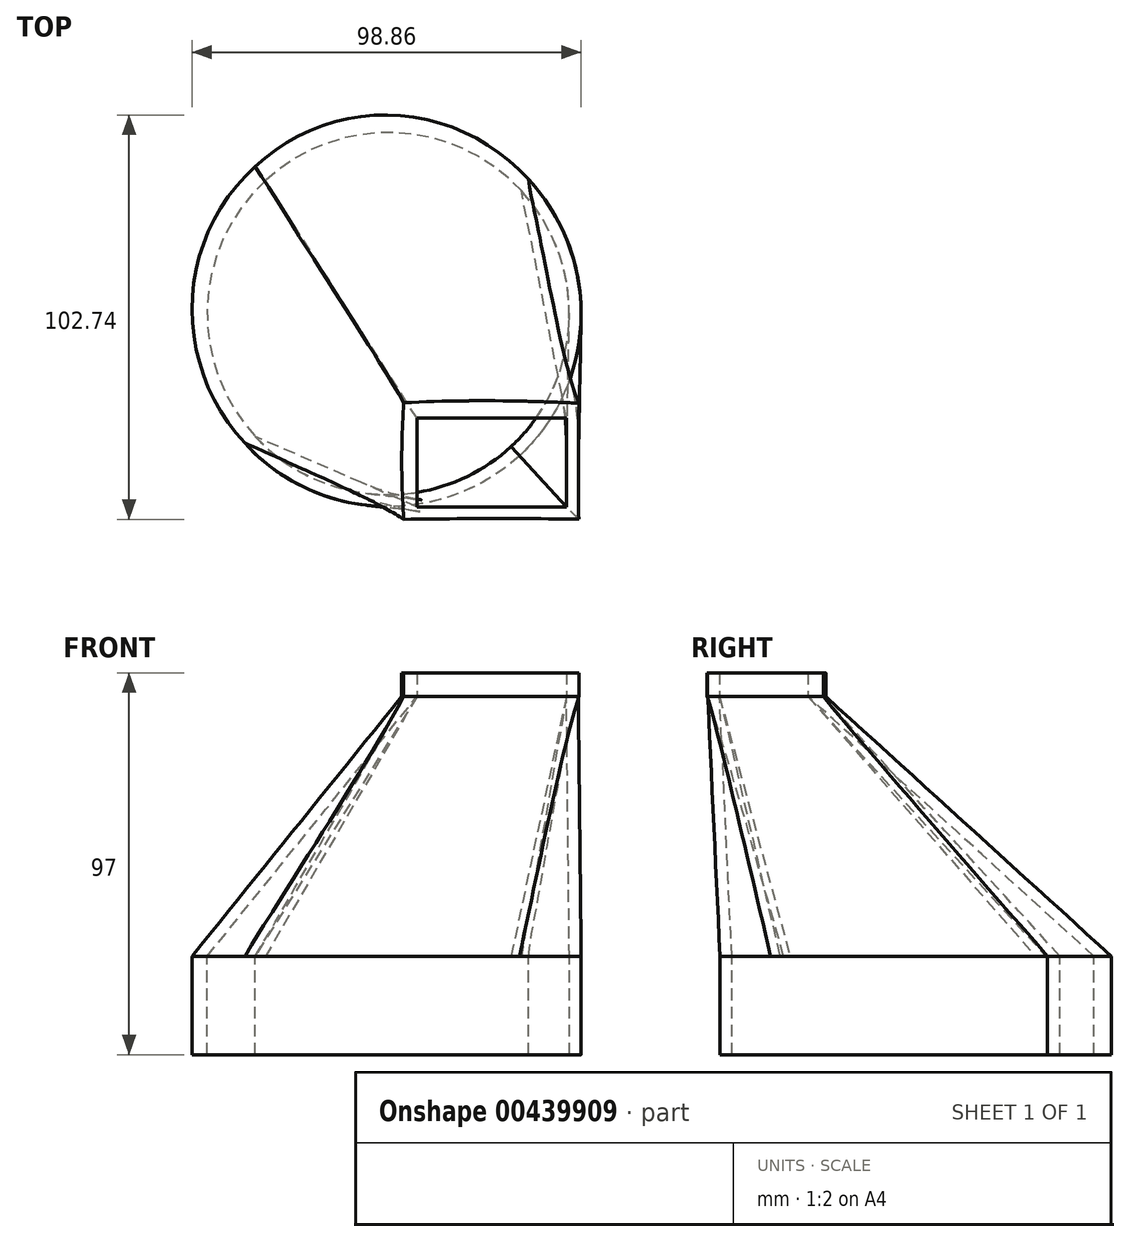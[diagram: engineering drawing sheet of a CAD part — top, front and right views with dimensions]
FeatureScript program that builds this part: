
annotation { "Feature Type Name" : "Feature", "Feature Type Description" : "" }
export const myFeature = defineFeature(function(context is Context, id is Id, definition is map)
    precondition{}
    {
        {
            var Q0;
            Q0=qCreatedBy(makeId("Top.planeOp"),FACE);
            cPlane(context, id + "F0", {"entities" : qUnion([Q0]), "cplaneType" : CPlaneType.OFFSET, "offset" : 66 * mm, "width" : 150 * mm, "height" : 150 * mm});
        }
        {
            var Q0;
            Q0=qCreatedBy(makeId("Top.planeOp"),FACE);
            var sketch = newSketch(context, id + "F1", { "sketchPlane" : qUnion([Q0])});
            skCircle(sketch, "E0", {"center": v(0, 0) * mm, "radius": 46 * mm});
            skSolve(sketch);
        }
        {
            var Q0;
            Q0=qCreatedBy(id+"F0.planeOp",FACE);
            var sketch = newSketch(context, id + "F2", { "sketchPlane" : qUnion([Q0])});
            skLineSegment(sketch, "E1.bottom", {"start": v(45.29, -49.1) * mm, "end": v(7.29, -49.1) * mm});
            skLineSegment(sketch, "E1.top", {"start": v(45.29, -26.6) * mm, "end": v(7.29, -26.6) * mm});
            skLineSegment(sketch, "E1.left", {"start": v(45.29, -49.1) * mm, "end": v(45.29, -26.6) * mm});
            skLineSegment(sketch, "E1.right", {"start": v(7.29, -49.1) * mm, "end": v(7.29, -26.6) * mm});
            skSolve(sketch);
        }
        {
            var Q0;
            Q0=makeQuery(id+"F2.imprint","IMPRINT",FACE,{"disambiguationData":[TD([[makeQuery(id+"F2.imprint","IMPRINT",EDGE,{"derivedFrom":sQuery(id+"F2.wireOp",EDGE,"E1.bottom")}),-1.0]])]});
            var Q1;
            Q1=makeQuery(id+"F1.imprint","IMPRINT",FACE,{"disambiguationData":[TD([[makeQuery(id+"F1.imprint","IMPRINT",EDGE,{"derivedFrom":sQuery(id+"F1.wireOp",EDGE,"E0")}),1.0]])]});
            loft(context, id + "F3", {"sheetProfilesArray" : [{ "sheetProfileEntities" : qUnion([Q0]) }, { "sheetProfileEntities" : qUnion([Q1]) }]});
        }
        {
            var Q0;
            Q0=makeQuery(id+"F3.opLoft","CAP_FACE",FACE,{"disambiguationData":[OSD([makeQuery(id+"F2.imprint","IMPRINT",FACE,{"disambiguationData":[TD([[makeQuery(id+"F2.imprint","IMPRINT",EDGE,{"derivedFrom":sQuery(id+"F2.wireOp",EDGE,"E1.bottom")}),-1.0]])]})])],"isStart":true});
            var Q1;
            Q1=makeQuery(id+"F3.opLoft","CAP_FACE",FACE,{"disambiguationData":[OSD([makeQuery(id+"F1.imprint","IMPRINT",FACE,{"disambiguationData":[TD([[makeQuery(id+"F1.imprint","IMPRINT",EDGE,{"derivedFrom":sQuery(id+"F1.wireOp",EDGE,"E0")}),1.0]])]})])],"isStart":true});
            shell(context, id + "F4", {"entities" : qUnion([Q0, Q1]), "thickness" : 3 * mm, "oppositeDirection" : true});
        }
        {
            var Q0;
            Q0=makeQuery(id+"F3.opLoft","CAP_FACE",FACE,{"disambiguationData":[OSD([makeQuery(id+"F2.imprint","IMPRINT",FACE,{"disambiguationData":[TD([[makeQuery(id+"F2.imprint","IMPRINT",EDGE,{"derivedFrom":sQuery(id+"F2.wireOp",EDGE,"E1.bottom")}),-1.0]])]})])],"isStart":true});
            extrude(context, id + "F5", {"entities" : qUnion([Q0]), "operationType" : NewBodyOperationType.ADD, "depth" : 6 * mm});
        }
        {
            var Q0;
            Q0=makeQuery(id+"F3.opLoft","CAP_FACE",FACE,{"disambiguationData":[OSD([makeQuery(id+"F1.imprint","IMPRINT",FACE,{"disambiguationData":[TD([[makeQuery(id+"F1.imprint","IMPRINT",EDGE,{"derivedFrom":sQuery(id+"F1.wireOp",EDGE,"E0")}),1.0]])]})])],"isStart":true});
            extrude(context, id + "F6", {"entities" : qUnion([Q0]), "operationType" : NewBodyOperationType.ADD, "depth" : 25 * mm});
        }
    });
